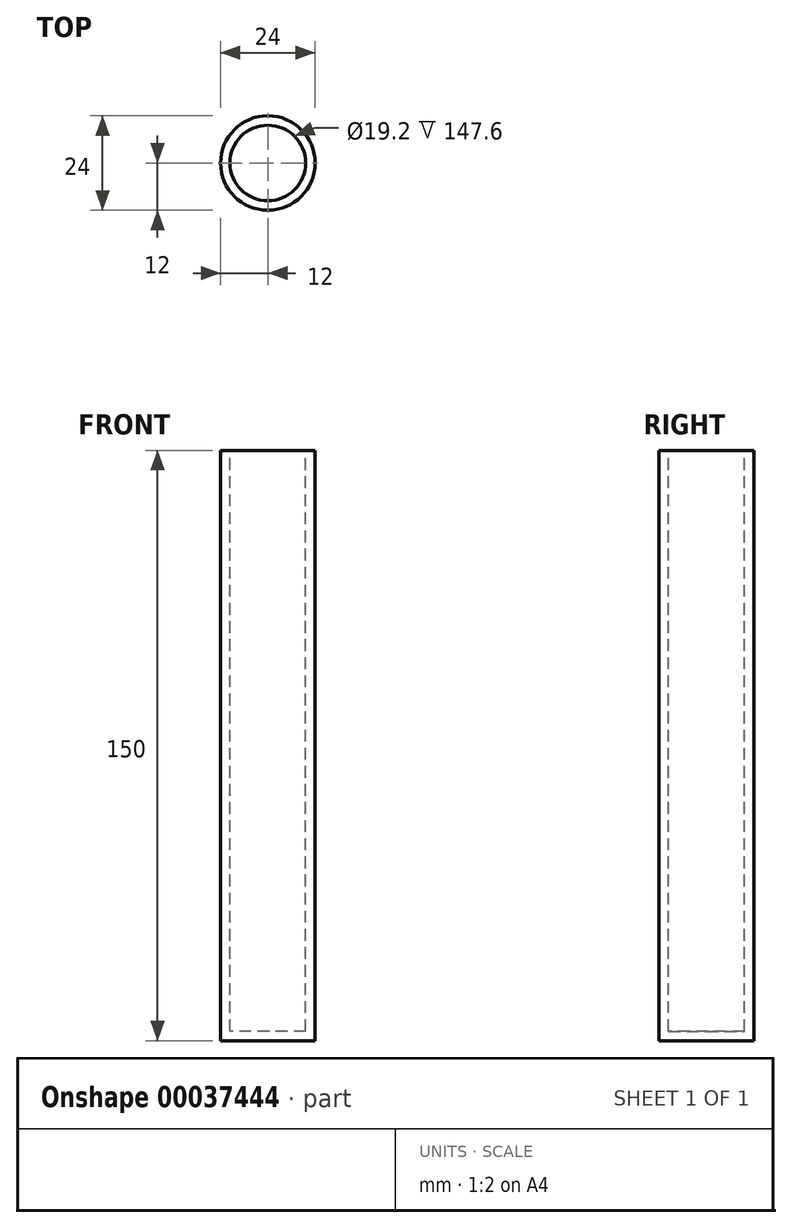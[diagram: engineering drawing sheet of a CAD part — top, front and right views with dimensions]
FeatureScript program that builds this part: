
annotation { "Feature Type Name" : "Feature", "Feature Type Description" : "" }
export const myFeature = defineFeature(function(context is Context, id is Id, definition is map)
    precondition{}
    {
        {
            var Q0;
            Q0=qCreatedBy(makeId("Front.planeOp"),FACE);
            var sketch = newSketch(context, id + "F0", { "sketchPlane" : qUnion([Q0])});
            skLineSegment(sketch, "E0", {"start": v(0, 137.3) * mm, "end": v(0, -107.95) * mm});
            skLineSegment(sketch, "E1", {"start": v(0, 0) * mm, "end": v(-12, 0) * mm});
            skLineSegment(sketch, "E2", {"start": v(-12, 0) * mm, "end": v(-12, 150) * mm});
            skLineSegment(sketch, "E3", {"start": v(-12, 150) * mm, "end": v(0, 150) * mm});
            skLineSegment(sketch, "E4", {"start": v(0, 150) * mm, "end": v(0, 0) * mm});
            skSolve(sketch);
        }
        {
            var Q0;
            Q0 = qSketchRegion(id + "F0", true);
            var Q1;
            Q1=sQuery(id+"F0.wireOp",EDGE,"E0");
            revolve(context, id + "F1", {"entities" : qUnion([Q0]), "axis" : qUnion([Q1]), "revolveType" : RevolveType.FULL});
        }
        {
            var Q0;
            Q0=makeQuery(id+"F1.opRevolve","SWEPT_FACE",FACE,{"disambiguationData":[OSD([sQuery(id+"F0.wireOp",EDGE,"E3")])]});
            shell(context, id + "F2", {"entities" : qUnion([Q0]), "thickness" : 2.4 * mm});
        }
    });
